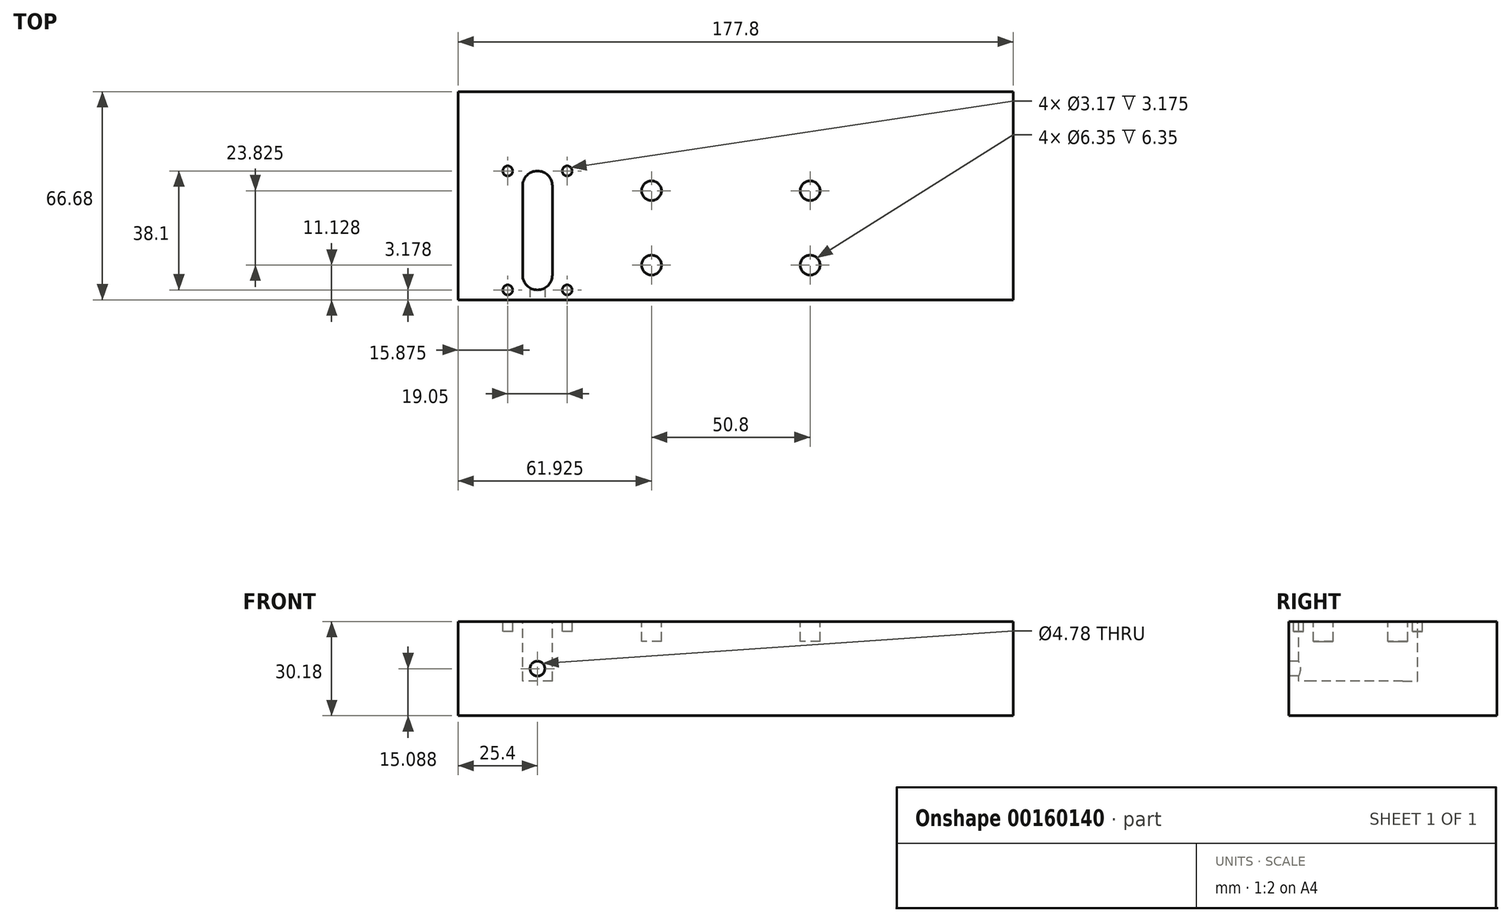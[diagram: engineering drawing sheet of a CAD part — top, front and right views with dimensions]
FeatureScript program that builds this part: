
annotation { "Feature Type Name" : "Feature", "Feature Type Description" : "" }
export const myFeature = defineFeature(function(context is Context, id is Id, definition is map)
    precondition{}
    {
        {
            var Q0;
            Q0=qCreatedBy(makeId("Top.planeOp"),FACE);
            var sketch = newSketch(context, id + "F0", { "sketchPlane" : qUnion([Q0])});
            skLineSegment(sketch, "E0.bottom", {"start": v(88.9, -33.34) * mm, "end": v(-88.9, -33.34) * mm});
            skLineSegment(sketch, "E0.top", {"start": v(88.9, 33.34) * mm, "end": v(-88.9, 33.34) * mm});
            skLineSegment(sketch, "E0.left", {"start": v(88.9, -33.34) * mm, "end": v(88.9, 33.34) * mm});
            skLineSegment(sketch, "E0.right", {"start": v(-88.9, -33.34) * mm, "end": v(-88.9, 33.34) * mm});
            skPoint(sketch, "E0.middle", {"position": v(0, 0) * mm});
            skSolve(sketch);
        }
        {
            var Q0;
            Q0=makeQuery(id+"F0.imprint","IMPRINT",FACE,{"disambiguationData":[TD([[makeQuery(id+"F0.imprint","IMPRINT",EDGE,{"derivedFrom":sQuery(id+"F0.wireOp",EDGE,"E0.bottom")}),-1.0]])]});
            extrude(context, id + "F1", {"entities" : qUnion([Q0]), "depth" : 30.18 * mm});
        }
        {
            var Q0;
            Q0=makeQuery(id+"F1.opExtrude","CAP_FACE",FACE,{"disambiguationData":[OSD([sQuery(id+"F0.wireOp",EDGE,"E0.bottom"),sQuery(id+"F0.wireOp",EDGE,"E0.top"),sQuery(id+"F0.wireOp",EDGE,"E0.left"),sQuery(id+"F0.wireOp",EDGE,"E0.right")])],"isStart":false});
            var sketch = newSketch(context, id + "F2", { "sketchPlane" : qUnion([Q0])});
            skLineSegment(sketch, "E1", {"start": v(-83.11, 7.94) * mm, "end": v(-47.18, 7.94) * mm, "construction": true});
            skLineSegment(sketch, "E2", {"start": v(-83.06, -30.16) * mm, "end": v(-44.78, -30.16) * mm, "construction": true});
            skLineSegment(sketch, "E3", {"start": v(-73.03, 7.94) * mm, "end": v(-73.03, -30.16) * mm, "construction": true});
            skLineSegment(sketch, "E4", {"start": v(-53.98, 7.94) * mm, "end": v(-53.98, -30.16) * mm, "construction": true});
            skCircle(sketch, "E5", {"center": v(-73.03, 7.94) * mm, "radius": 1.59 * mm});
            skCircle(sketch, "E6", {"center": v(-53.98, 7.94) * mm, "radius": 1.59 * mm});
            skCircle(sketch, "E7", {"center": v(-53.98, -30.16) * mm, "radius": 1.59 * mm});
            skCircle(sketch, "E8", {"center": v(-73.03, -30.16) * mm, "radius": 1.59 * mm});
            skLineSegment(sketch, "E9", {"start": v(-63.5, 14.1) * mm, "end": v(-63.5, -41.04) * mm, "construction": true});
            skLineSegment(sketch, "E10", {"start": v(-80.06, 0) * mm, "end": v(-45.28, 0) * mm, "construction": true});
            skLineSegment(sketch, "E11", {"start": v(-77.14, -23.03) * mm, "end": v(-43.97, -23.03) * mm, "construction": true});
            skSolve(sketch);
        }
        {
            var Q0;
            Q0 = qSketchRegion(id + "F2", true);
            extrude(context, id + "F3", {"entities" : qUnion([Q0]), "operationType" : NewBodyOperationType.REMOVE, "oppositeDirection" : true, "depth" : 3.17 * mm});
        }
        {
            var Q0;
            Q0=makeQuery(id+"F1.opExtrude","CAP_FACE",FACE,{"disambiguationData":[OSD([sQuery(id+"F0.wireOp",EDGE,"E0.bottom"),sQuery(id+"F0.wireOp",EDGE,"E0.top"),sQuery(id+"F0.wireOp",EDGE,"E0.left"),sQuery(id+"F0.wireOp",EDGE,"E0.right")])],"isStart":false});
            var sketch = newSketch(context, id + "F4", { "sketchPlane" : qUnion([Q0])});
            skLineSegment(sketch, "E12", {"start": v(-73.03, 7.94) * mm, "end": v(-53.98, 7.94) * mm, "construction": true});
            skLineSegment(sketch, "E13", {"start": v(-73.03, -30.16) * mm, "end": v(-53.98, -30.16) * mm, "construction": true});
            skLineSegment(sketch, "E14", {"start": v(-63.5, 7.94) * mm, "end": v(-63.5, -30.16) * mm, "construction": true});
            skLineSegment(sketch, "E15", {"start": v(-73.23, 3.16) * mm, "end": v(-50.48, 3.16) * mm, "construction": true});
            skLineSegment(sketch, "E16", {"start": v(-71.24, -25.39) * mm, "end": v(-51.24, -25.39) * mm, "construction": true});
            skArc(sketch, "E17", {"start": v(-58.74, 3.16) * mm, "mid": v(-63.5, 7.92) * mm, "end": v(-68.26, 3.16) * mm});
            skArc(sketch, "E18", {"start": v(-68.26, -25.39) * mm, "mid": v(-63.5, -30.15) * mm, "end": v(-58.74, -25.39) * mm});
            skLineSegment(sketch, "E19", {"start": v(-58.74, 3.16) * mm, "end": v(-58.74, -25.39) * mm});
            skLineSegment(sketch, "E20", {"start": v(-68.26, 3.16) * mm, "end": v(-68.26, -25.39) * mm});
            skSolve(sketch);
        }
        {
            var Q0;
            Q0 = qSketchRegion(id + "F4", true);
            extrude(context, id + "F5", {"entities" : qUnion([Q0]), "operationType" : NewBodyOperationType.REMOVE, "oppositeDirection" : true, "depth" : 19.05 * mm});
        }
        {
            var Q0;
            Q0=makeQuery(id+"F1.opExtrude","CAP_FACE",FACE,{"disambiguationData":[OSD([sQuery(id+"F0.wireOp",EDGE,"E0.bottom"),sQuery(id+"F0.wireOp",EDGE,"E0.top"),sQuery(id+"F0.wireOp",EDGE,"E0.left"),sQuery(id+"F0.wireOp",EDGE,"E0.right")])],"isStart":false});
            var sketch = newSketch(context, id + "F6", { "sketchPlane" : qUnion([Q0])});
            skLineSegment(sketch, "E21", {"start": v(-30.2, 1.61) * mm, "end": v(75.82, 1.61) * mm, "construction": true});
            skLineSegment(sketch, "E22", {"start": v(-30.72, -22.21) * mm, "end": v(68.82, -22.21) * mm, "construction": true});
            skLineSegment(sketch, "E23", {"start": v(-26.97, 19.48) * mm, "end": v(-26.97, -45.85) * mm, "construction": true});
            skLineSegment(sketch, "E24", {"start": v(23.83, 17.66) * mm, "end": v(23.83, -44.55) * mm, "construction": true});
            skCircle(sketch, "E25", {"center": v(-26.97, 1.61) * mm, "radius": 3.18 * mm});
            skCircle(sketch, "E26", {"center": v(23.83, 1.61) * mm, "radius": 3.18 * mm});
            skCircle(sketch, "E27", {"center": v(23.83, -22.21) * mm, "radius": 3.18 * mm});
            skCircle(sketch, "E28", {"center": v(-26.97, -22.21) * mm, "radius": 3.18 * mm});
            skSolve(sketch);
        }
        {
            var Q0;
            Q0 = qSketchRegion(id + "F6", true);
            extrude(context, id + "F7", {"entities" : qUnion([Q0]), "operationType" : NewBodyOperationType.REMOVE, "oppositeDirection" : true, "depth" : 6.35 * mm});
        }
        {
            var Q0;
            Q0=makeQuery(id+"F1.opExtrude","SWEPT_FACE",FACE,{"disambiguationData":[OSD([sQuery(id+"F0.wireOp",EDGE,"E0.bottom")])]});
            var sketch = newSketch(context, id + "F8", { "sketchPlane" : qUnion([Q0])});
            skLineSegment(sketch, "E29", {"start": v(-88.9, 15.09) * mm, "end": v(-2.48, 15.09) * mm, "construction": true});
            skLineSegment(sketch, "E30", {"start": v(-63.5, 37.98) * mm, "end": v(-63.5, -9.5) * mm, "construction": true});
            skCircle(sketch, "E31", {"center": v(-63.5, 15.09) * mm, "radius": 2.39 * mm});
            skSolve(sketch);
        }
        {
            var Q0;
            Q0 = qSketchRegion(id + "F8", true);
            extrude(context, id + "F9", {"entities" : qUnion([Q0]), "operationType" : NewBodyOperationType.REMOVE, "oppositeDirection" : true, "depth" : 6.35 * mm});
        }
    });
